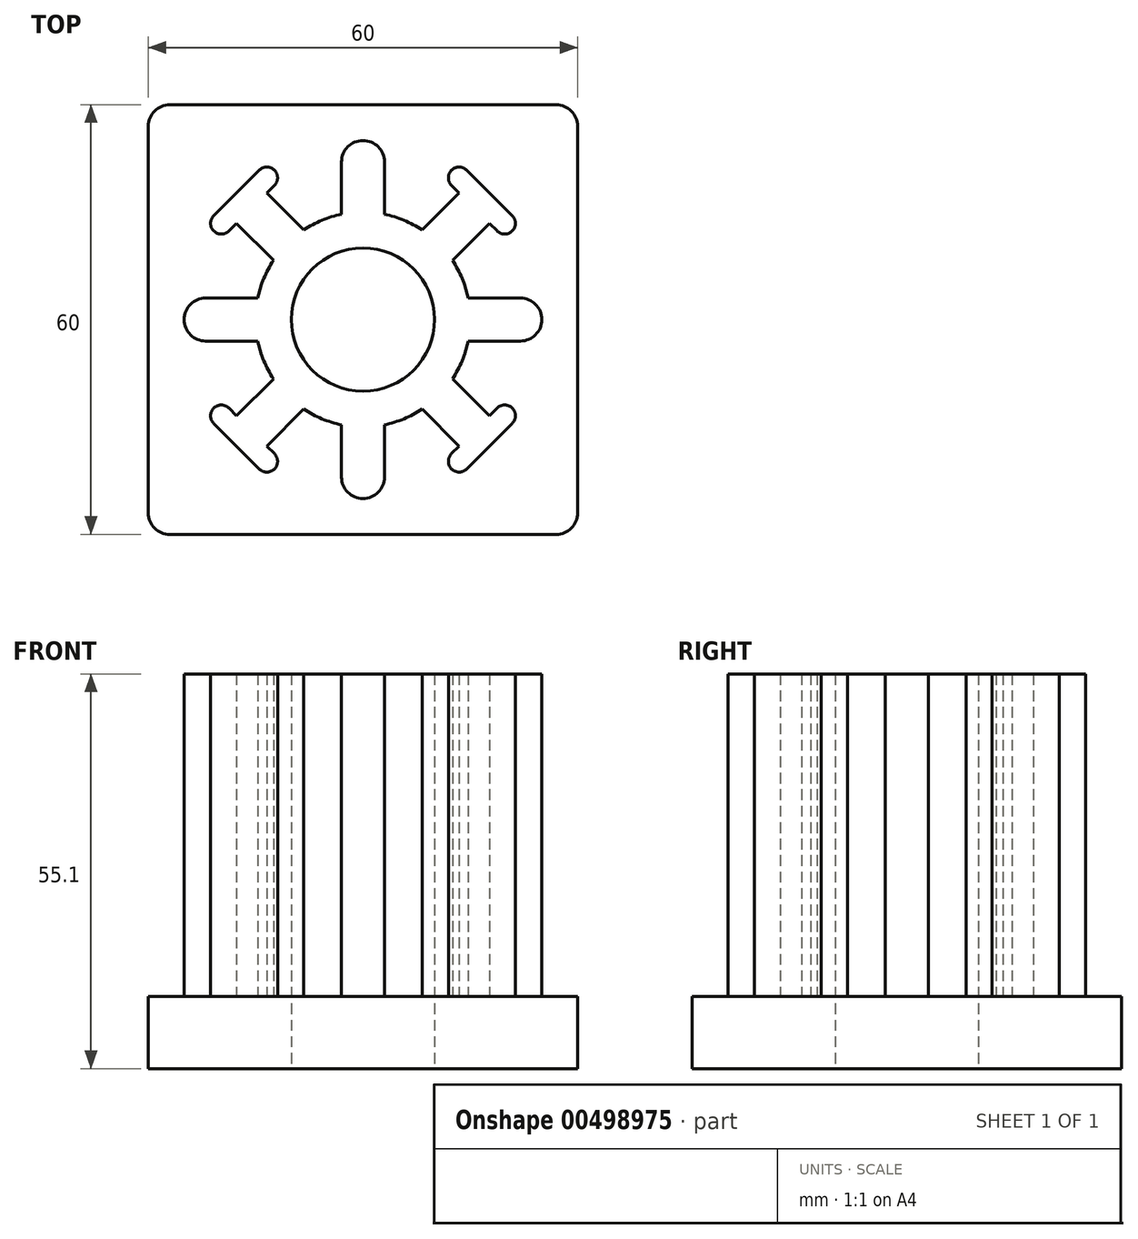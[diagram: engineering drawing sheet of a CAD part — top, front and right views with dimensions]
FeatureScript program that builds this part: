
annotation { "Feature Type Name" : "Feature", "Feature Type Description" : "" }
export const myFeature = defineFeature(function(context is Context, id is Id, definition is map)
    precondition{}
    {
        {
            var Q0;
            Q0=qCreatedBy(makeId("Top.planeOp"),FACE);
            var sketch = newSketch(context, id + "F0", { "sketchPlane" : qUnion([Q0])});
            skLineSegment(sketch, "E0.bottom", {"start": v(-30, 30) * mm, "end": v(30, 30) * mm});
            skLineSegment(sketch, "E0.top", {"start": v(-30, -30) * mm, "end": v(30, -30) * mm});
            skLineSegment(sketch, "E0.left", {"start": v(-30, 30) * mm, "end": v(-30, -30) * mm});
            skLineSegment(sketch, "E0.right", {"start": v(30, 30) * mm, "end": v(30, -30) * mm});
            skSolve(sketch);
        }
        {
            var Q0;
            Q0 = qSketchRegion(id + "F0", true);
            extrude(context, id + "F1", {"entities" : qUnion([Q0]), "depth" : 10.1 * mm});
        }
        {
            var Q0;
            Q0=makeQuery(id+"F1.opExtrude","SWEPT_EDGE",EDGE,{"disambiguationData":[OSD([sQuery(id+"F0.wireOp",EDGE,"E0.top"),sQuery(id+"F0.wireOp",EDGE,"E0.right")])]});
            var Q1;
            Q1=makeQuery(id+"F1.opExtrude","SWEPT_EDGE",EDGE,{"disambiguationData":[OSD([sQuery(id+"F0.wireOp",EDGE,"E0.bottom"),sQuery(id+"F0.wireOp",EDGE,"E0.right")])]});
            var Q2;
            Q2=makeQuery(id+"F1.opExtrude","SWEPT_EDGE",EDGE,{"disambiguationData":[OSD([sQuery(id+"F0.wireOp",EDGE,"E0.top"),sQuery(id+"F0.wireOp",EDGE,"E0.left")])]});
            var Q3;
            Q3=makeQuery(id+"F1.opExtrude","SWEPT_EDGE",EDGE,{"disambiguationData":[OSD([sQuery(id+"F0.wireOp",EDGE,"E0.bottom"),sQuery(id+"F0.wireOp",EDGE,"E0.left")])]});
            fillet(context, id + "F2", {"entities" : qUnion([Q0, Q1, Q2, Q3]), "radius" : 3 * mm, "tangentPropagation" : true, "allowEdgeOverflow" : false});
        }
        {
            var Q0;
            Q0=makeQuery(id+"F1.opExtrude","CAP_FACE",FACE,{"disambiguationData":[OSD([sQuery(id+"F0.wireOp",EDGE,"E0.bottom"),sQuery(id+"F0.wireOp",EDGE,"E0.top"),sQuery(id+"F0.wireOp",EDGE,"E0.left"),sQuery(id+"F0.wireOp",EDGE,"E0.right")])],"isStart":false});
            var sketch = newSketch(context, id + "F3", { "sketchPlane" : qUnion([Q0])});
            skLineSegment(sketch, "E1", {"start": v(0, 0) * mm, "end": v(-73.02, 0) * mm, "construction": true});
            skLineSegment(sketch, "E2", {"start": v(0, 0) * mm, "end": v(0, 73.02) * mm, "construction": true});
            skArc(sketch, "E3", {"start": v(-7.07, 7.07) * mm, "mid": v(-9.24, 3.83) * mm, "end": v(-10, 0) * mm});
            skArc(sketch, "E4", {"start": v(-12.51, 8.27) * mm, "mid": v(-13.86, 5.74) * mm, "end": v(-14.7, 3) * mm});
            skLineSegment(sketch, "E5", {"start": v(-25, 0) * mm, "end": v(-25, 0) * mm});
            skLineSegment(sketch, "E6", {"start": v(-22, 3) * mm, "end": v(-14.7, 3) * mm});
            skPoint(sketch, "E7.visualSharp", {"position": v(-25, 3) * mm});
            skArc(sketch, "E7.filletArc", {"start": v(-22, 3) * mm, "mid": v(-24.12, 2.12) * mm, "end": v(-25, 0) * mm});
            skLineSegment(sketch, "E8", {"start": v(0, 0) * mm, "end": v(-20.33, 20.33) * mm, "construction": true});
            skLineSegment(sketch, "E9", {"start": v(-20.86, 14.5) * mm, "end": v(-17.68, 17.68) * mm});
            skLineSegment(sketch, "E10", {"start": v(-20.86, 12.37) * mm, "end": v(-20.86, 12.37) * mm});
            skPoint(sketch, "E10.endSnap0", {"position": v(-19.8, 15.56) * mm});
            skLineSegment(sketch, "E11", {"start": v(-18.74, 12.37) * mm, "end": v(-17.68, 13.44) * mm});
            skLineSegment(sketch, "E12", {"start": v(-17.68, 13.44) * mm, "end": v(-12.51, 8.27) * mm});
            skPoint(sketch, "E13.visualSharp", {"position": v(-21.92, 13.44) * mm});
            skArc(sketch, "E13.filletArc", {"start": v(-20.86, 14.5) * mm, "mid": v(-21.3, 13.44) * mm, "end": v(-20.86, 12.37) * mm});
            skPoint(sketch, "E14.visualSharp", {"position": v(-19.8, 11.31) * mm});
            skArc(sketch, "E14.filletArc", {"start": v(-20.86, 12.37) * mm, "mid": v(-19.8, 11.94) * mm, "end": v(-18.74, 12.37) * mm});
            skPoint(sketch, "E15.MirrorP", {"position": v(-15.56, 19.8) * mm});
            skLineSegment(sketch, "E16.MirrorCS", {"start": v(-14.5, 20.86) * mm, "end": v(-17.68, 17.68) * mm});
            skPoint(sketch, "E17.MirrorP", {"position": v(-13.44, 21.92) * mm});
            skArc(sketch, "E18.MirrorCS", {"start": v(-12.37, 20.86) * mm, "mid": v(-11.94, 19.8) * mm, "end": v(-12.37, 18.74) * mm});
            skLineSegment(sketch, "E19.MirrorCS", {"start": v(-12.37, 18.74) * mm, "end": v(-13.44, 17.68) * mm});
            skArc(sketch, "E20.MirrorCS", {"start": v(-14.5, 20.86) * mm, "mid": v(-13.44, 21.3) * mm, "end": v(-12.37, 20.86) * mm});
            skLineSegment(sketch, "E21.MirrorCS", {"start": v(-13.44, 17.68) * mm, "end": v(-8.27, 12.51) * mm});
            skArc(sketch, "E22.MirrorCS", {"start": v(-8.27, 12.51) * mm, "mid": v(-5.74, 13.86) * mm, "end": v(-3, 14.7) * mm});
            skLineSegment(sketch, "E23.MirrorCS", {"start": v(-3, 22) * mm, "end": v(-3, 14.7) * mm});
            skArc(sketch, "E24.MirrorCS", {"start": v(-3, 22) * mm, "mid": v(-2.12, 24.12) * mm, "end": v(0, 25) * mm});
            skArc(sketch, "E25.MirrorCS", {"start": v(-7.07, 7.07) * mm, "mid": v(-3.83, 9.24) * mm, "end": v(0, 10) * mm});
            skArc(sketch, "E26.MirrorCS", {"start": v(14.5, 20.86) * mm, "mid": v(13.44, 21.3) * mm, "end": v(12.37, 20.86) * mm});
            skLineSegment(sketch, "E27.MirrorCS", {"start": v(12.37, 18.74) * mm, "end": v(13.44, 17.68) * mm});
            skArc(sketch, "E28.MirrorCS", {"start": v(12.37, 20.86) * mm, "mid": v(11.94, 19.8) * mm, "end": v(12.37, 18.74) * mm});
            skLineSegment(sketch, "E29.MirrorCS", {"start": v(18.74, 12.37) * mm, "end": v(17.68, 13.44) * mm});
            skArc(sketch, "E30.MirrorCS", {"start": v(20.86, 14.5) * mm, "mid": v(21.3, 13.44) * mm, "end": v(20.86, 12.37) * mm});
            skArc(sketch, "E31.MirrorCS", {"start": v(20.86, 12.37) * mm, "mid": v(19.8, 11.94) * mm, "end": v(18.74, 12.37) * mm});
            skArc(sketch, "E32.MirrorCS", {"start": v(22, 3) * mm, "mid": v(24.12, 2.12) * mm, "end": v(25, 0) * mm});
            skLineSegment(sketch, "E33.MirrorCS", {"start": v(20.86, 14.5) * mm, "end": v(17.68, 17.68) * mm});
            skLineSegment(sketch, "E34.MirrorCS", {"start": v(14.5, 20.86) * mm, "end": v(17.68, 17.68) * mm});
            skLineSegment(sketch, "E35.MirrorCS", {"start": v(13.44, 17.68) * mm, "end": v(8.27, 12.51) * mm});
            skArc(sketch, "E36.MirrorCS", {"start": v(7.07, 7.07) * mm, "mid": v(9.24, 3.83) * mm, "end": v(10, 0) * mm});
            skPoint(sketch, "E37.MirrorP", {"position": v(19.8, 15.56) * mm});
            skLineSegment(sketch, "E38.MirrorCS", {"start": v(3, 22) * mm, "end": v(3, 14.7) * mm});
            skArc(sketch, "E39.MirrorCS", {"start": v(12.51, 8.27) * mm, "mid": v(13.86, 5.74) * mm, "end": v(14.7, 3) * mm});
            skLineSegment(sketch, "E40.MirrorCS", {"start": v(20.86, 12.37) * mm, "end": v(20.86, 12.37) * mm});
            skLineSegment(sketch, "E41.MirrorCS", {"start": v(22, 3) * mm, "end": v(14.7, 3) * mm});
            skPoint(sketch, "E42.MirrorP", {"position": v(15.56, 19.8) * mm});
            skPoint(sketch, "E43.MirrorP", {"position": v(13.44, 21.92) * mm});
            skLineSegment(sketch, "E44.MirrorCS", {"start": v(0, 0) * mm, "end": v(20.33, 20.33) * mm, "construction": true});
            skPoint(sketch, "E45.MirrorP", {"position": v(19.8, 11.31) * mm});
            skArc(sketch, "E46.MirrorCS", {"start": v(7.07, 7.07) * mm, "mid": v(3.83, 9.24) * mm, "end": v(0, 10) * mm});
            skLineSegment(sketch, "E47.MirrorCS", {"start": v(25, 0) * mm, "end": v(25, 0) * mm});
            skArc(sketch, "E48.MirrorCS", {"start": v(8.27, 12.51) * mm, "mid": v(5.74, 13.86) * mm, "end": v(3, 14.7) * mm});
            skPoint(sketch, "E49.MirrorP", {"position": v(21.92, 13.44) * mm});
            skArc(sketch, "E50.MirrorCS", {"start": v(3, 22) * mm, "mid": v(2.12, 24.12) * mm, "end": v(0, 25) * mm});
            skPoint(sketch, "E51.MirrorP", {"position": v(25, 3) * mm});
            skLineSegment(sketch, "E52.MirrorCS", {"start": v(17.68, 13.44) * mm, "end": v(12.51, 8.27) * mm});
            skArc(sketch, "E53.MirrorCS", {"start": v(12.37, -20.86) * mm, "mid": v(11.94, -19.8) * mm, "end": v(12.37, -18.74) * mm});
            skArc(sketch, "E54.MirrorCS", {"start": v(20.86, -12.37) * mm, "mid": v(19.8, -11.94) * mm, "end": v(18.74, -12.37) * mm});
            skArc(sketch, "E55.MirrorCS", {"start": v(-20.86, -12.37) * mm, "mid": v(-19.8, -11.94) * mm, "end": v(-18.74, -12.37) * mm});
            skArc(sketch, "E56.MirrorCS", {"start": v(-20.86, -14.5) * mm, "mid": v(-21.3, -13.44) * mm, "end": v(-20.86, -12.37) * mm});
            skLineSegment(sketch, "E57.MirrorCS", {"start": v(-18.74, -12.37) * mm, "end": v(-17.68, -13.44) * mm});
            skArc(sketch, "E58.MirrorCS", {"start": v(20.86, -14.5) * mm, "mid": v(21.3, -13.44) * mm, "end": v(20.86, -12.37) * mm});
            skLineSegment(sketch, "E59.MirrorCS", {"start": v(12.37, -18.74) * mm, "end": v(13.44, -17.68) * mm});
            skLineSegment(sketch, "E60.MirrorCS", {"start": v(-12.37, -18.74) * mm, "end": v(-13.44, -17.68) * mm});
            skArc(sketch, "E61.MirrorCS", {"start": v(-14.5, -20.86) * mm, "mid": v(-13.44, -21.3) * mm, "end": v(-12.37, -20.86) * mm});
            skLineSegment(sketch, "E62.MirrorCS", {"start": v(18.74, -12.37) * mm, "end": v(17.68, -13.44) * mm});
            skArc(sketch, "E63.MirrorCS", {"start": v(14.5, -20.86) * mm, "mid": v(13.44, -21.3) * mm, "end": v(12.37, -20.86) * mm});
            skArc(sketch, "E64.MirrorCS", {"start": v(-12.37, -20.86) * mm, "mid": v(-11.94, -19.8) * mm, "end": v(-12.37, -18.74) * mm});
            skLineSegment(sketch, "E65.MirrorCS", {"start": v(14.5, -20.86) * mm, "end": v(17.68, -17.68) * mm});
            skArc(sketch, "E66.MirrorCS", {"start": v(22, -3) * mm, "mid": v(24.12, -2.12) * mm, "end": v(25, 0) * mm});
            skLineSegment(sketch, "E67.MirrorCS", {"start": v(-14.5, -20.86) * mm, "end": v(-17.68, -17.68) * mm});
            skLineSegment(sketch, "E68.MirrorCS", {"start": v(-20.86, -14.5) * mm, "end": v(-17.68, -17.68) * mm});
            skArc(sketch, "E69.MirrorCS", {"start": v(-22, -3) * mm, "mid": v(-24.12, -2.12) * mm, "end": v(-25, 0) * mm});
            skLineSegment(sketch, "E70.MirrorCS", {"start": v(20.86, -14.5) * mm, "end": v(17.68, -17.68) * mm});
            skLineSegment(sketch, "E71.MirrorCS", {"start": v(-13.44, -17.68) * mm, "end": v(-8.27, -12.51) * mm});
            skArc(sketch, "E72.MirrorCS", {"start": v(7.07, -7.07) * mm, "mid": v(3.83, -9.24) * mm, "end": v(0, -10) * mm});
            skArc(sketch, "E73.MirrorCS", {"start": v(-7.07, -7.07) * mm, "mid": v(-3.83, -9.24) * mm, "end": v(0, -10) * mm});
            skLineSegment(sketch, "E74.MirrorCS", {"start": v(17.68, -13.44) * mm, "end": v(12.51, -8.27) * mm});
            skLineSegment(sketch, "E75.MirrorCS", {"start": v(3, -22) * mm, "end": v(3, -14.7) * mm});
            skPoint(sketch, "E76.MirrorP", {"position": v(-19.8, -11.31) * mm});
            skPoint(sketch, "E77.MirrorP", {"position": v(-19.8, -15.56) * mm});
            skPoint(sketch, "E78.MirrorP", {"position": v(21.92, -13.44) * mm});
            skLineSegment(sketch, "E79.MirrorCS", {"start": v(0, 0) * mm, "end": v(20.33, -20.33) * mm, "construction": true});
            skPoint(sketch, "E80.MirrorP", {"position": v(-13.44, -21.92) * mm});
            skPoint(sketch, "E81.MirrorP", {"position": v(19.8, -11.31) * mm});
            skArc(sketch, "E82.MirrorCS", {"start": v(-3, -22) * mm, "mid": v(-2.12, -24.12) * mm, "end": v(0, -25) * mm});
            skLineSegment(sketch, "E83.MirrorCS", {"start": v(-17.68, -13.44) * mm, "end": v(-12.51, -8.27) * mm});
            skLineSegment(sketch, "E84.MirrorCS", {"start": v(0, 0) * mm, "end": v(-20.33, -20.33) * mm, "construction": true});
            skLineSegment(sketch, "E85.MirrorCS", {"start": v(-22, -3) * mm, "end": v(-14.7, -3) * mm});
            skPoint(sketch, "E86.MirrorP", {"position": v(19.8, -15.56) * mm});
            skPoint(sketch, "E87.MirrorP", {"position": v(25, -3) * mm});
            skArc(sketch, "E88.MirrorCS", {"start": v(-12.51, -8.27) * mm, "mid": v(-13.86, -5.74) * mm, "end": v(-14.7, -3) * mm});
            skLineSegment(sketch, "E89.MirrorCS", {"start": v(20.86, -12.37) * mm, "end": v(20.86, -12.37) * mm});
            skArc(sketch, "E90.MirrorCS", {"start": v(-7.07, -7.07) * mm, "mid": v(-9.24, -3.83) * mm, "end": v(-10, 0) * mm});
            skLineSegment(sketch, "E91.MirrorCS", {"start": v(0, 0) * mm, "end": v(0, -73.02) * mm, "construction": true});
            skPoint(sketch, "E92.MirrorP", {"position": v(-25, -3) * mm});
            skArc(sketch, "E93.MirrorCS", {"start": v(3, -22) * mm, "mid": v(2.12, -24.12) * mm, "end": v(0, -25) * mm});
            skArc(sketch, "E94.MirrorCS", {"start": v(12.51, -8.27) * mm, "mid": v(13.86, -5.74) * mm, "end": v(14.7, -3) * mm});
            skLineSegment(sketch, "E95.MirrorCS", {"start": v(22, -3) * mm, "end": v(14.7, -3) * mm});
            skPoint(sketch, "E96.MirrorP", {"position": v(15.56, -19.8) * mm});
            skArc(sketch, "E97.MirrorCS", {"start": v(-8.27, -12.51) * mm, "mid": v(-5.74, -13.86) * mm, "end": v(-3, -14.7) * mm});
            skLineSegment(sketch, "E98.MirrorCS", {"start": v(-3, -22) * mm, "end": v(-3, -14.7) * mm});
            skPoint(sketch, "E99.MirrorP", {"position": v(-21.92, -13.44) * mm});
            skPoint(sketch, "E100.MirrorP", {"position": v(-15.56, -19.8) * mm});
            skLineSegment(sketch, "E101.MirrorCS", {"start": v(-20.86, -12.37) * mm, "end": v(-20.86, -12.37) * mm});
            skArc(sketch, "E102.MirrorCS", {"start": v(8.27, -12.51) * mm, "mid": v(5.74, -13.86) * mm, "end": v(3, -14.7) * mm});
            skLineSegment(sketch, "E103.MirrorCS", {"start": v(13.44, -17.68) * mm, "end": v(8.27, -12.51) * mm});
            skArc(sketch, "E104.MirrorCS", {"start": v(7.07, -7.07) * mm, "mid": v(9.24, -3.83) * mm, "end": v(10, 0) * mm});
            skPoint(sketch, "E105.MirrorP", {"position": v(13.44, -21.92) * mm});
            skSolve(sketch);
        }
        {
            var Q0;
            Q0 = qSketchRegion(id + "F3", true);
            extrude(context, id + "F4", {"entities" : qUnion([Q0]), "operationType" : NewBodyOperationType.ADD, "depth" : 45 * mm});
        }
        {
            var Q0;
            Q0=makeQuery(id+"F1.opExtrude","CAP_FACE",FACE,{"disambiguationData":[OSD([sQuery(id+"F0.wireOp",EDGE,"E0.bottom"),sQuery(id+"F0.wireOp",EDGE,"E0.top"),sQuery(id+"F0.wireOp",EDGE,"E0.left"),sQuery(id+"F0.wireOp",EDGE,"E0.right")])],"isStart":true});
            var sketch = newSketch(context, id + "F5", { "sketchPlane" : qUnion([Q0])});
            skCircle(sketch, "E106", {"center": v(0, 0) * mm, "radius": 10 * mm});
            skSolve(sketch);
        }
        {
            var Q0;
            Q0 = qSketchRegion(id + "F5", true);
            extrude(context, id + "F6", {"entities" : qUnion([Q0]), "operationType" : NewBodyOperationType.REMOVE, "endBound" : BoundingType.UP_TO_NEXT, "oppositeDirection" : true, "depth" : 25 * mm});
        }
    });
